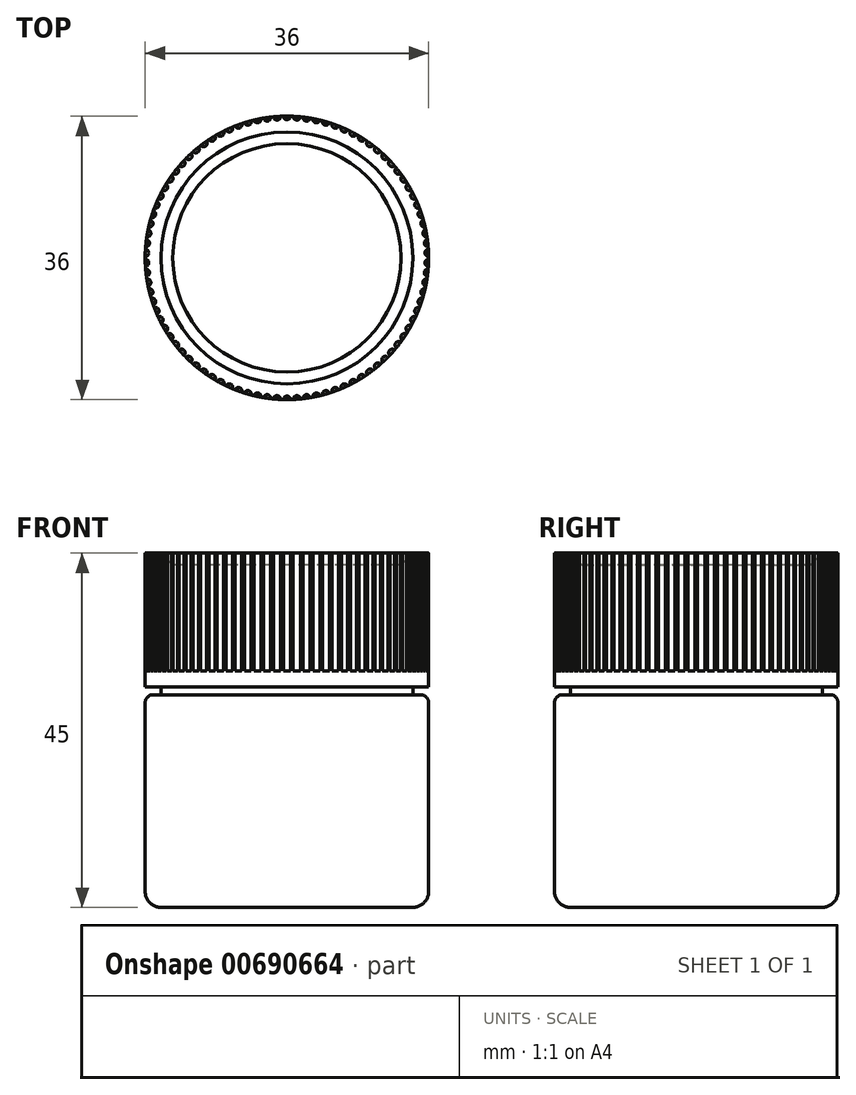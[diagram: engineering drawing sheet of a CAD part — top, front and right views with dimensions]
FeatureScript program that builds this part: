
annotation { "Feature Type Name" : "Feature", "Feature Type Description" : "" }
export const myFeature = defineFeature(function(context is Context, id is Id, definition is map)
    precondition{}
    {
        {
            var Q0;
            Q0=qCreatedBy(makeId("Top.planeOp"),FACE);
            var sketch = newSketch(context, id + "F0", { "sketchPlane" : qUnion([Q0])});
            skCircle(sketch, "E0", {"center": v(0, 0) * mm, "radius": 18 * mm});
            skSolve(sketch);
        }
        {
            var Q0;
            Q0=qSketchRegion(id+"F0",true);
            extrude(context, id + "F1", {"entities" : qUnion([Q0]), "depth" : 27 * mm, "offsetDistance" : 25 * mm});
        }
        {
            var Q0;
            Q0=makeQuery(id+"F1.opExtrude","CAP_FACE",FACE,{"disambiguationData":[OSD([sQuery(id+"F0.wireOp",EDGE,"E0")])],"isStart":false});
            var sketch = newSketch(context, id + "F2", { "sketchPlane" : qUnion([Q0])});
            skCircle(sketch, "E1", {"center": v(0, 0) * mm, "radius": 16 * mm});
            skSolve(sketch);
        }
        {
            var Q0;
            Q0=qSketchRegion(id+"F2",true);
            extrude(context, id + "F3", {"entities" : qUnion([Q0]), "operationType" : NewBodyOperationType.ADD, "depth" : 1 * mm, "offsetDistance" : 25 * mm});
        }
        {
            var Q0;
            Q0=makeQuery(id+"F3.opExtrude","CAP_FACE",FACE,{"disambiguationData":[OSD([sQuery(id+"F2.wireOp",EDGE,"E1")])],"isStart":false});
            var sketch = newSketch(context, id + "F4", { "sketchPlane" : qUnion([Q0])});
            skCircle(sketch, "E2", {"center": v(0, 0) * mm, "radius": 18 * mm});
            skSolve(sketch);
        }
        {
            var Q0;
            Q0=qSketchRegion(id+"F4",true);
            extrude(context, id + "F5", {"entities" : qUnion([Q0]), "operationType" : NewBodyOperationType.ADD, "depth" : 17 * mm, "offsetDistance" : 25 * mm});
        }
        {
            var Q0;
            Q0=makeQuery(id+"F1.opExtrude","CAP_FACE",FACE,{"disambiguationData":[OSD([sQuery(id+"F0.wireOp",EDGE,"E0")])],"isStart":true});
            fillet(context, id + "F6", {"entities" : qUnion([Q0]), "radius" : 2 * mm, "tangentPropagation" : true, "allowEdgeOverflow" : false});
        }
        {
            var Q0;
            Q0=makeQuery(id+"F1.opExtrude","CAP_EDGE",EDGE,{"disambiguationData":[OSD([sQuery(id+"F0.wireOp",EDGE,"E0")])],"isStart":false});
            var Q1;
            Q1=makeQuery(id+"F3.opExtrude","CAP_EDGE",EDGE,{"disambiguationData":[OSD([sQuery(id+"F2.wireOp",EDGE,"E1")])],"isStart":true});
            fillet(context, id + "F7", {"entities" : qUnion([Q0, Q1]), "radius" : 1 * mm, "tangentPropagation" : true, "allowEdgeOverflow" : false});
        }
        {
            var Q0;
            Q0=makeQuery(id+"F5.opExtrude","CAP_FACE",FACE,{"disambiguationData":[OSD([sQuery(id+"F4.wireOp",EDGE,"E2")])],"isStart":false});
            var sketch = newSketch(context, id + "F8", { "sketchPlane" : qUnion([Q0])});
            skCircle(sketch, "E3", {"center": v(0, 0) * mm, "radius": 16 * mm});
            skSolve(sketch);
        }
        {
            var Q0;
            Q0=qSketchRegion(id+"F8",true);
            extrude(context, id + "F9", {"entities" : qUnion([Q0]), "operationType" : NewBodyOperationType.REMOVE, "oppositeDirection" : true, "depth" : 1.5 * mm, "offsetDistance" : 25 * mm, "hasDraft" : true, "draftAngle" : 45 * degree, "draftPullDirection" : true});
        }
        {
            var Q0;
            Q0=makeQuery(id+"F5.opExtrude","CAP_FACE",FACE,{"disambiguationData":[OSD([sQuery(id+"F4.wireOp",EDGE,"E2")])],"isStart":false});
            var sketch = newSketch(context, id + "F10", { "sketchPlane" : qUnion([Q0])});
            skCircle(sketch, "E4", {"center": v(0, 18) * mm, "radius": 0.45 * mm});
            skCircle(sketch, "E5.1.0", {"center": v(-1.26, 17.96) * mm, "radius": 0.45 * mm});
            skCircle(sketch, "E5.2.0", {"center": v(-2.5, 17.82) * mm, "radius": 0.45 * mm});
            skCircle(sketch, "E5.3.0", {"center": v(-3.74, 17.6) * mm, "radius": 0.45 * mm});
            skCircle(sketch, "E5.4.0", {"center": v(-4.96, 17.3) * mm, "radius": 0.45 * mm});
            skCircle(sketch, "E5.5.0", {"center": v(-6.16, 16.91) * mm, "radius": 0.45 * mm});
            skCircle(sketch, "E5.6.0", {"center": v(-7.32, 16.44) * mm, "radius": 0.45 * mm});
            skCircle(sketch, "E5.7.0", {"center": v(-8.45, 15.9) * mm, "radius": 0.45 * mm});
            skCircle(sketch, "E5.8.0", {"center": v(-9.54, 15.26) * mm, "radius": 0.45 * mm});
            skCircle(sketch, "E5.9.0", {"center": v(-10.58, 14.56) * mm, "radius": 0.45 * mm});
            skCircle(sketch, "E5.10.0", {"center": v(-11.57, 13.79) * mm, "radius": 0.45 * mm});
            skCircle(sketch, "E5.11.0", {"center": v(-12.5, 12.95) * mm, "radius": 0.45 * mm});
            skCircle(sketch, "E5.12.0", {"center": v(-13.38, 12.04) * mm, "radius": 0.45 * mm});
            skCircle(sketch, "E5.13.0", {"center": v(-14.18, 11.08) * mm, "radius": 0.45 * mm});
            skCircle(sketch, "E5.14.0", {"center": v(-14.92, 10.07) * mm, "radius": 0.45 * mm});
            skCircle(sketch, "E5.15.0", {"center": v(-15.59, 9) * mm, "radius": 0.45 * mm});
            skCircle(sketch, "E5.16.0", {"center": v(-16.18, 7.9) * mm, "radius": 0.45 * mm});
            skCircle(sketch, "E5.17.0", {"center": v(-16.69, 6.74) * mm, "radius": 0.45 * mm});
            skCircle(sketch, "E5.18.0", {"center": v(-17.12, 5.56) * mm, "radius": 0.45 * mm});
            skCircle(sketch, "E5.19.0", {"center": v(-17.47, 4.35) * mm, "radius": 0.45 * mm});
            skCircle(sketch, "E5.20.0", {"center": v(-17.73, 3.13) * mm, "radius": 0.45 * mm});
            skCircle(sketch, "E5.21.0", {"center": v(-17.9, 1.88) * mm, "radius": 0.45 * mm});
            skCircle(sketch, "E5.22.0", {"center": v(-17.99, 0.63) * mm, "radius": 0.45 * mm});
            skCircle(sketch, "E5.23.0", {"center": v(-17.99, -0.63) * mm, "radius": 0.45 * mm});
            skCircle(sketch, "E5.24.0", {"center": v(-17.9, -1.88) * mm, "radius": 0.45 * mm});
            skCircle(sketch, "E5.25.0", {"center": v(-17.73, -3.13) * mm, "radius": 0.45 * mm});
            skCircle(sketch, "E5.26.0", {"center": v(-17.47, -4.35) * mm, "radius": 0.45 * mm});
            skCircle(sketch, "E5.27.0", {"center": v(-17.12, -5.56) * mm, "radius": 0.45 * mm});
            skCircle(sketch, "E5.28.0", {"center": v(-16.69, -6.74) * mm, "radius": 0.45 * mm});
            skCircle(sketch, "E5.29.0", {"center": v(-16.18, -7.9) * mm, "radius": 0.45 * mm});
            skCircle(sketch, "E5.30.0", {"center": v(-15.59, -9) * mm, "radius": 0.45 * mm});
            skCircle(sketch, "E5.31.0", {"center": v(-14.92, -10.07) * mm, "radius": 0.45 * mm});
            skCircle(sketch, "E5.32.0", {"center": v(-14.18, -11.08) * mm, "radius": 0.45 * mm});
            skCircle(sketch, "E5.33.0", {"center": v(-13.38, -12.04) * mm, "radius": 0.45 * mm});
            skCircle(sketch, "E5.34.0", {"center": v(-12.5, -12.95) * mm, "radius": 0.45 * mm});
            skCircle(sketch, "E5.35.0", {"center": v(-11.57, -13.79) * mm, "radius": 0.45 * mm});
            skCircle(sketch, "E5.36.0", {"center": v(-10.58, -14.56) * mm, "radius": 0.45 * mm});
            skCircle(sketch, "E5.37.0", {"center": v(-9.54, -15.26) * mm, "radius": 0.45 * mm});
            skCircle(sketch, "E5.38.0", {"center": v(-8.45, -15.9) * mm, "radius": 0.45 * mm});
            skCircle(sketch, "E5.39.0", {"center": v(-7.32, -16.44) * mm, "radius": 0.45 * mm});
            skCircle(sketch, "E5.40.0", {"center": v(-6.16, -16.91) * mm, "radius": 0.45 * mm});
            skCircle(sketch, "E5.41.0", {"center": v(-4.96, -17.3) * mm, "radius": 0.45 * mm});
            skCircle(sketch, "E5.42.0", {"center": v(-3.74, -17.6) * mm, "radius": 0.45 * mm});
            skCircle(sketch, "E5.43.0", {"center": v(-2.5, -17.82) * mm, "radius": 0.45 * mm});
            skCircle(sketch, "E5.44.0", {"center": v(-1.26, -17.96) * mm, "radius": 0.45 * mm});
            skCircle(sketch, "E5.45.0", {"center": v(0, -18) * mm, "radius": 0.45 * mm});
            skCircle(sketch, "E5.46.0", {"center": v(1.26, -17.96) * mm, "radius": 0.45 * mm});
            skCircle(sketch, "E5.47.0", {"center": v(2.5, -17.82) * mm, "radius": 0.45 * mm});
            skCircle(sketch, "E5.48.0", {"center": v(3.74, -17.6) * mm, "radius": 0.45 * mm});
            skCircle(sketch, "E5.49.0", {"center": v(4.96, -17.3) * mm, "radius": 0.45 * mm});
            skCircle(sketch, "E5.50.0", {"center": v(6.16, -16.91) * mm, "radius": 0.45 * mm});
            skCircle(sketch, "E5.51.0", {"center": v(7.32, -16.44) * mm, "radius": 0.45 * mm});
            skCircle(sketch, "E5.52.0", {"center": v(8.45, -15.9) * mm, "radius": 0.45 * mm});
            skCircle(sketch, "E5.53.0", {"center": v(9.54, -15.26) * mm, "radius": 0.45 * mm});
            skCircle(sketch, "E5.54.0", {"center": v(10.58, -14.56) * mm, "radius": 0.45 * mm});
            skCircle(sketch, "E5.55.0", {"center": v(11.57, -13.79) * mm, "radius": 0.45 * mm});
            skCircle(sketch, "E5.56.0", {"center": v(12.5, -12.95) * mm, "radius": 0.45 * mm});
            skCircle(sketch, "E5.57.0", {"center": v(13.38, -12.04) * mm, "radius": 0.45 * mm});
            skCircle(sketch, "E5.58.0", {"center": v(14.18, -11.08) * mm, "radius": 0.45 * mm});
            skCircle(sketch, "E5.59.0", {"center": v(14.92, -10.07) * mm, "radius": 0.45 * mm});
            skCircle(sketch, "E5.60.0", {"center": v(15.59, -9) * mm, "radius": 0.45 * mm});
            skCircle(sketch, "E5.61.0", {"center": v(16.18, -7.9) * mm, "radius": 0.45 * mm});
            skCircle(sketch, "E5.62.0", {"center": v(16.69, -6.74) * mm, "radius": 0.45 * mm});
            skCircle(sketch, "E5.63.0", {"center": v(17.12, -5.56) * mm, "radius": 0.45 * mm});
            skCircle(sketch, "E5.64.0", {"center": v(17.47, -4.35) * mm, "radius": 0.45 * mm});
            skCircle(sketch, "E5.65.0", {"center": v(17.73, -3.13) * mm, "radius": 0.45 * mm});
            skCircle(sketch, "E5.66.0", {"center": v(17.9, -1.88) * mm, "radius": 0.45 * mm});
            skCircle(sketch, "E5.67.0", {"center": v(17.99, -0.63) * mm, "radius": 0.45 * mm});
            skCircle(sketch, "E5.68.0", {"center": v(17.99, 0.63) * mm, "radius": 0.45 * mm});
            skCircle(sketch, "E5.69.0", {"center": v(17.9, 1.88) * mm, "radius": 0.45 * mm});
            skCircle(sketch, "E5.70.0", {"center": v(17.73, 3.13) * mm, "radius": 0.45 * mm});
            skCircle(sketch, "E5.71.0", {"center": v(17.47, 4.35) * mm, "radius": 0.45 * mm});
            skCircle(sketch, "E5.72.0", {"center": v(17.12, 5.56) * mm, "radius": 0.45 * mm});
            skCircle(sketch, "E5.73.0", {"center": v(16.69, 6.74) * mm, "radius": 0.45 * mm});
            skCircle(sketch, "E5.74.0", {"center": v(16.18, 7.9) * mm, "radius": 0.45 * mm});
            skCircle(sketch, "E5.75.0", {"center": v(15.59, 9) * mm, "radius": 0.45 * mm});
            skCircle(sketch, "E5.76.0", {"center": v(14.92, 10.07) * mm, "radius": 0.45 * mm});
            skCircle(sketch, "E5.77.0", {"center": v(14.18, 11.08) * mm, "radius": 0.45 * mm});
            skCircle(sketch, "E5.78.0", {"center": v(13.38, 12.04) * mm, "radius": 0.45 * mm});
            skCircle(sketch, "E5.79.0", {"center": v(12.5, 12.95) * mm, "radius": 0.45 * mm});
            skCircle(sketch, "E5.80.0", {"center": v(11.57, 13.79) * mm, "radius": 0.45 * mm});
            skCircle(sketch, "E5.81.0", {"center": v(10.58, 14.56) * mm, "radius": 0.45 * mm});
            skCircle(sketch, "E5.82.0", {"center": v(9.54, 15.26) * mm, "radius": 0.45 * mm});
            skCircle(sketch, "E5.83.0", {"center": v(8.45, 15.9) * mm, "radius": 0.45 * mm});
            skCircle(sketch, "E5.84.0", {"center": v(7.32, 16.44) * mm, "radius": 0.45 * mm});
            skCircle(sketch, "E5.85.0", {"center": v(6.16, 16.91) * mm, "radius": 0.45 * mm});
            skCircle(sketch, "E5.86.0", {"center": v(4.96, 17.3) * mm, "radius": 0.45 * mm});
            skCircle(sketch, "E5.87.0", {"center": v(3.74, 17.6) * mm, "radius": 0.45 * mm});
            skCircle(sketch, "E5.88.0", {"center": v(2.5, 17.82) * mm, "radius": 0.45 * mm});
            skCircle(sketch, "E5.89.0", {"center": v(1.26, 17.96) * mm, "radius": 0.45 * mm});
            skPoint(sketch, "E5.center", {"position": v(0, 0) * mm});
            skSolve(sketch);
        }
        {
            var Q0;
            Q0=qSketchRegion(id+"F10",true);
            extrude(context, id + "F11", {"entities" : qUnion([Q0]), "operationType" : NewBodyOperationType.REMOVE, "oppositeDirection" : true, "depth" : 15 * mm, "offsetDistance" : 25 * mm});
        }
    });
